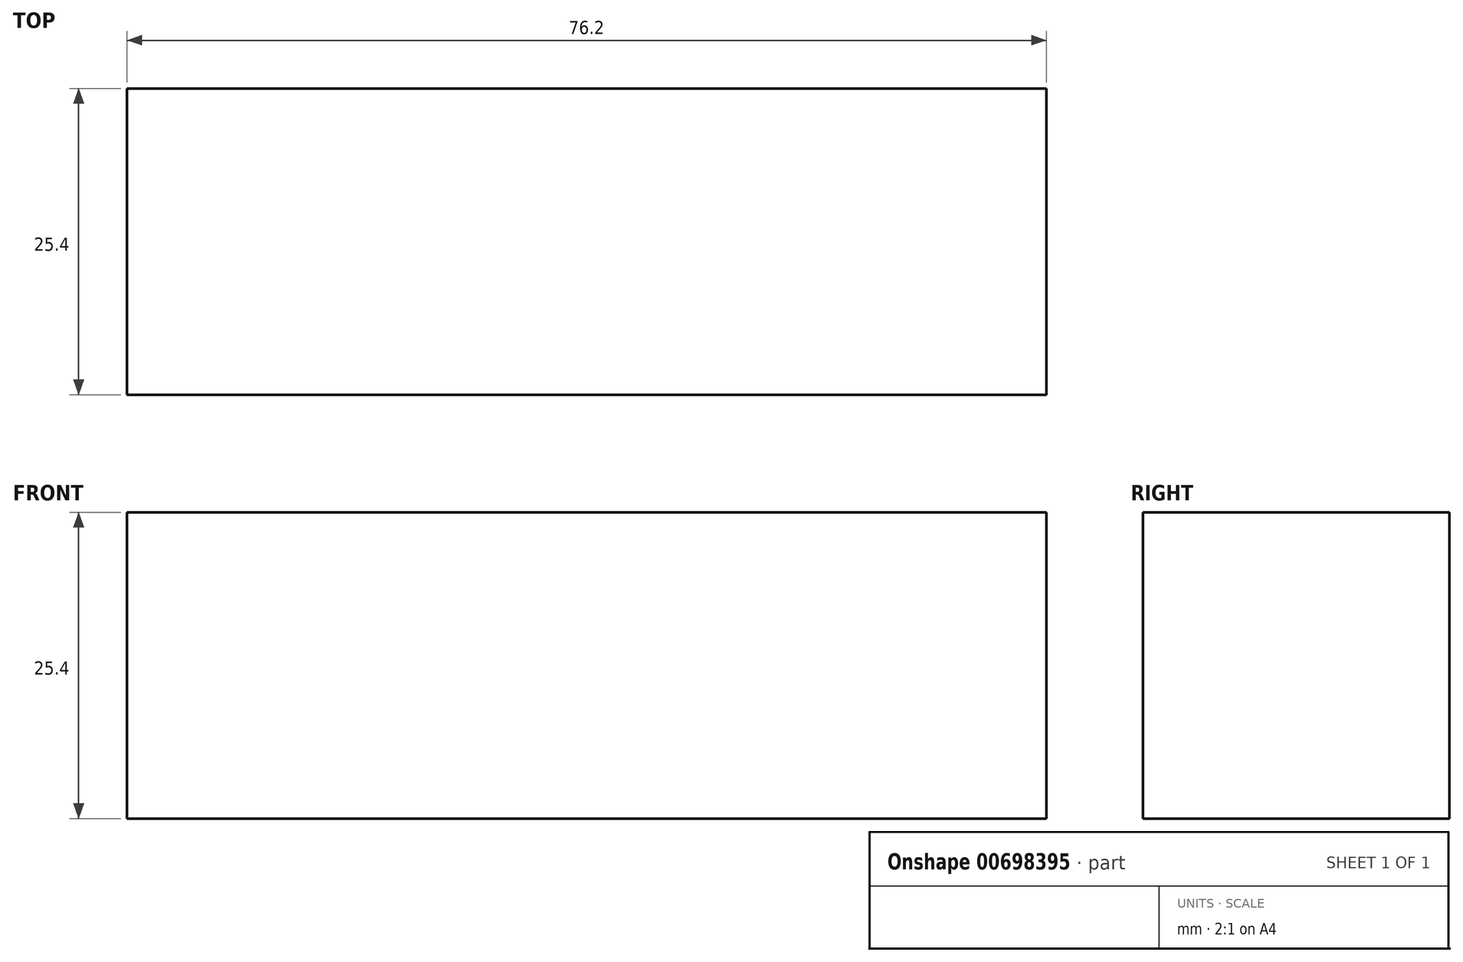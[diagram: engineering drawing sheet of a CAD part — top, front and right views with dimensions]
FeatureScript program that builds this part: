
annotation { "Feature Type Name" : "Feature", "Feature Type Description" : "" }
export const myFeature = defineFeature(function(context is Context, id is Id, definition is map)
    precondition{}
    {
        {
            var Q0;
            Q0=qCreatedBy(makeId("Front.planeOp"),FACE);
            var sketch = newSketch(context, id + "F0", { "sketchPlane" : qUnion([Q0])});
            skLineSegment(sketch, "E0.bottom", {"start": v(0, 0) * mm, "end": v(25.4, 0) * mm});
            skLineSegment(sketch, "E0.top", {"start": v(0, 25.4) * mm, "end": v(25.4, 25.4) * mm});
            skLineSegment(sketch, "E0.left", {"start": v(0, 0) * mm, "end": v(0, 25.4) * mm});
            skLineSegment(sketch, "E0.right", {"start": v(25.4, 0) * mm, "end": v(25.4, 25.4) * mm});
            skLineSegment(sketch, "E1.bottom", {"start": v(0, 25.4) * mm, "end": v(-25.4, 25.4) * mm});
            skLineSegment(sketch, "E1.top", {"start": v(0, 0) * mm, "end": v(-25.4, 0) * mm});
            skLineSegment(sketch, "E1.left", {"start": v(0, 25.4) * mm, "end": v(0, 0) * mm});
            skLineSegment(sketch, "E1.right", {"start": v(-25.4, 25.4) * mm, "end": v(-25.4, 0) * mm});
            skLineSegment(sketch, "E2.bottom", {"start": v(-25.4, 25.4) * mm, "end": v(-50.8, 25.4) * mm});
            skLineSegment(sketch, "E2.top", {"start": v(-25.4, 0) * mm, "end": v(-50.8, 0) * mm});
            skLineSegment(sketch, "E2.right", {"start": v(-50.8, 25.4) * mm, "end": v(-50.8, 0) * mm});
            skLineSegment(sketch, "E3.bottom", {"start": v(-25.4, 25.4) * mm, "end": v(0, 25.4) * mm});
            skLineSegment(sketch, "E3.top", {"start": v(-25.4, 50.8) * mm, "end": v(0, 50.8) * mm});
            skLineSegment(sketch, "E3.left", {"start": v(-25.4, 25.4) * mm, "end": v(-25.4, 50.8) * mm});
            skLineSegment(sketch, "E3.right", {"start": v(0, 25.4) * mm, "end": v(0, 50.8) * mm});
            skSolve(sketch);
        }
        {
            var Q0;
            Q0=makeQuery(id+"F0.imprint","IMPRINT",FACE,{"disambiguationData":[TD([[makeQuery(id+"F0.imprint","IMPRINT",EDGE,{"derivedFrom":sQuery(id+"F0.wireOp",EDGE,"E3.bottom")}),1.0]])]});
            var Q1;
            Q1=makeQuery(id+"F0.imprint","IMPRINT",FACE,{"disambiguationData":[TD([[makeQuery(id+"F0.imprint","IMPRINT",EDGE,{"derivedFrom":sQuery(id+"F0.wireOp",EDGE,"E2.bottom")}),1.0]])]});
            var Q2;
            Q2=makeQuery(id+"F0.imprint","IMPRINT",FACE,{"disambiguationData":[TD([[makeQuery(id+"F0.imprint","IMPRINT",EDGE,{"derivedFrom":sQuery(id+"F0.wireOp",EDGE,"E1.top")}),-1.0]])]});
            var Q3;
            Q3=makeQuery(id+"F0.imprint","IMPRINT",FACE,{"disambiguationData":[TD([[makeQuery(id+"F0.imprint","IMPRINT",EDGE,{"derivedFrom":sQuery(id+"F0.wireOp",EDGE,"E0.bottom")}),1.0]])]});
            extrude(context, id + "F1", {"entities" : qUnion([Q0, Q1, Q2, Q3]), "depth" : 25.4 * mm, "offsetDistance" : 25.4 * mm});
        }
    });
